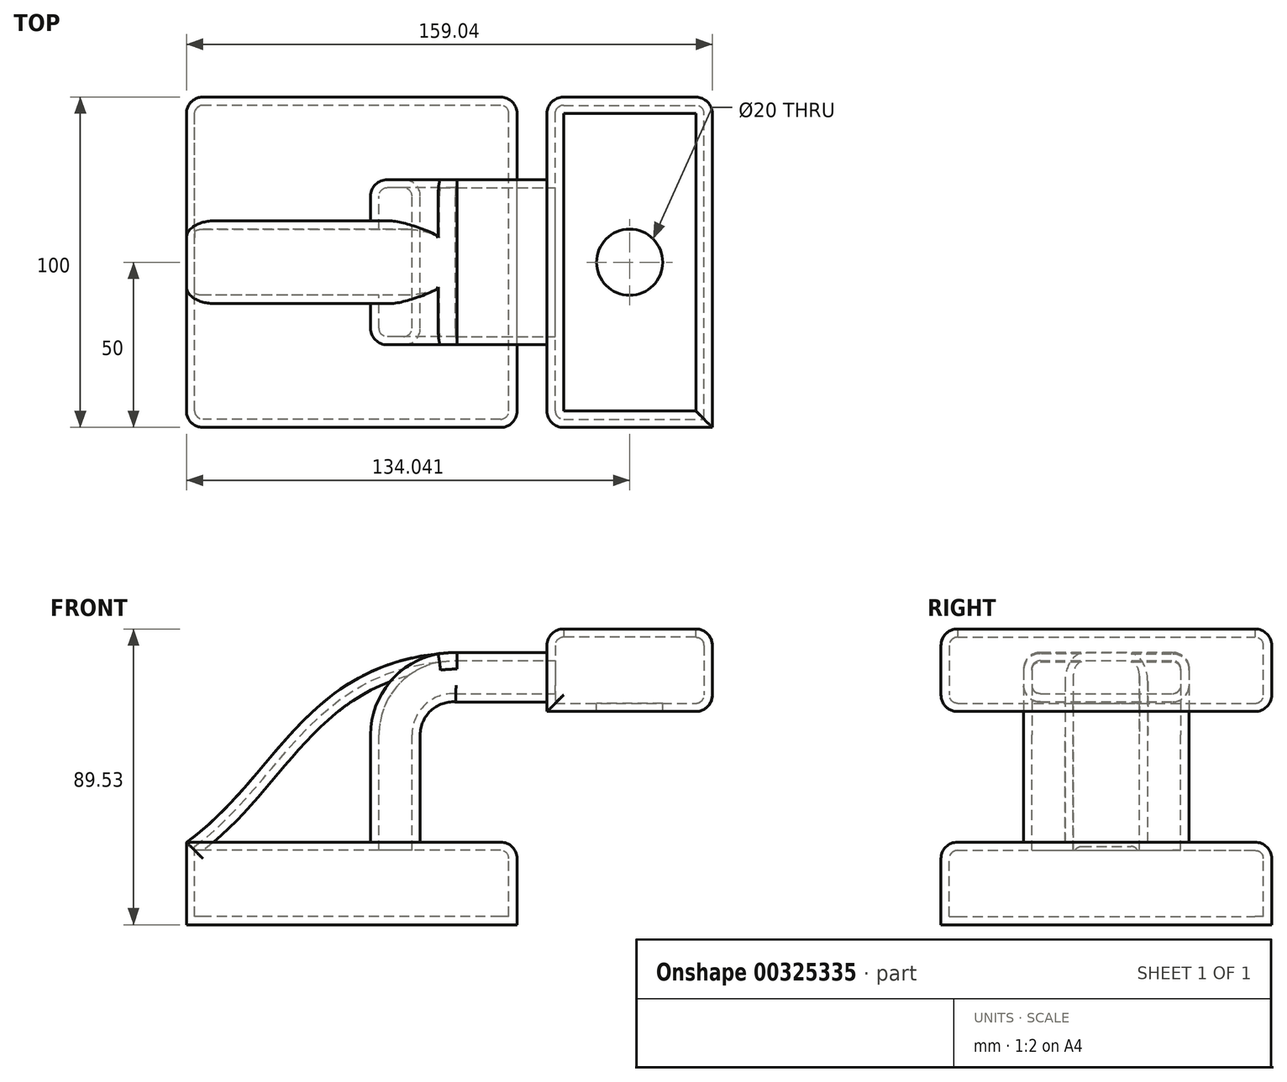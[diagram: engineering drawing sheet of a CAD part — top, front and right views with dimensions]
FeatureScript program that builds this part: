
annotation { "Feature Type Name" : "Feature", "Feature Type Description" : "" }
export const myFeature = defineFeature(function(context is Context, id is Id, definition is map)
    precondition{}
    {
        {
            var Q0;
            Q0=qCreatedBy(makeId("Front.planeOp"),FACE);
            var sketch = newSketch(context, id + "F0", { "sketchPlane" : qUnion([Q0])});
            skLineSegment(sketch, "E0.bottom", {"start": v(50, -12.5) * mm, "end": v(-50, -12.5) * mm});
            skLineSegment(sketch, "E0.top", {"start": v(50, 12.5) * mm, "end": v(-50, 12.5) * mm});
            skLineSegment(sketch, "E0.left", {"start": v(50, -12.5) * mm, "end": v(50, 12.5) * mm});
            skLineSegment(sketch, "E0.right", {"start": v(-50, -12.5) * mm, "end": v(-50, 12.5) * mm});
            skPoint(sketch, "E0.middle", {"position": v(0, 0) * mm});
            skLineSegment(sketch, "E1.bottom", {"start": v(59.04, 77.03) * mm, "end": v(109.04, 77.03) * mm});
            skLineSegment(sketch, "E1.top", {"start": v(59.04, 52.03) * mm, "end": v(109.04, 52.03) * mm});
            skLineSegment(sketch, "E1.left", {"start": v(59.04, 77.03) * mm, "end": v(59.04, 52.03) * mm});
            skLineSegment(sketch, "E1.right", {"start": v(109.04, 77.03) * mm, "end": v(109.04, 52.03) * mm});
            skPoint(sketch, "E1.middle", {"position": v(84.04, 64.53) * mm});
            skLineSegment(sketch, "E2", {"start": v(20.7, 12.5) * mm, "end": v(20.7, 44.96) * mm});
            skArc(sketch, "E3", {"start": v(20.7, 44.96) * mm, "mid": v(23.88, 52.27) * mm, "end": v(31.4, 54.94) * mm});
            skLineSegment(sketch, "E4", {"start": v(31.4, 54.94) * mm, "end": v(59.04, 54.94) * mm});
            skLineSegment(sketch, "E5.0", {"start": v(31.8, 69.94) * mm, "end": v(59.04, 69.94) * mm});
            skArc(sketch, "E5.1", {"start": v(5.7, 44.96) * mm, "mid": v(13.42, 63.02) * mm, "end": v(31.8, 69.94) * mm});
            skLineSegment(sketch, "E5.2", {"start": v(5.7, 12.5) * mm, "end": v(5.7, 44.96) * mm});
            skFitSpline(sketch, "E6", {"points": [v(-50, 12.5) * mm, v(31.8, 69.94) * mm], "startDerivative": vector(81.8, 57.44) * mm, "endDerivative": vector(137.66, 4.95) * mm});
            skSolve(sketch);
        }
        {
            var Q0;
            Q0=makeQuery(id+"F0.imprint","IMPRINT",FACE,{"disambiguationData":[TD([[makeQuery(id+"F0.imprint","IMPRINT",EDGE,{"derivedFrom":sQuery(id+"F0.wireOp",EDGE,"E0.bottom")}),-1.0]])]});
            extrude(context, id + "F1", {"entities" : qUnion([Q0]), "depth" : 100 * mm, "symmetric" : true});
        }
        {
            var Q0;
            {var subQ0=sQuery(id+"F0.wireOp",EDGE,"E2");Q0=makeQuery(id+"F0.imprint","IMPRINT",FACE,{"disambiguationData":[TD([[makeQuery(id+"F0.imprint","IMPRINT",EDGE,{"derivedFrom":subQ0}),1.0]])]});}
            extrude(context, id + "F2", {"entities" : qUnion([Q0]), "operationType" : NewBodyOperationType.ADD, "depth" : 50 * mm, "symmetric" : true});
        }
        {
            var Q0;
            {var subQ3=sQuery(id+"F0.wireOp",EDGE,"E5.2");Q0=makeQuery(id+"F0.imprint","IMPRINT",FACE,{"disambiguationData":[TD([[makeQuery(id+"F0.imprint","IMPRINT",EDGE,{"derivedFrom":subQ3}),1.0]])]});}
            extrude(context, id + "F3", {"entities" : qUnion([Q0]), "operationType" : NewBodyOperationType.ADD, "depth" : 25 * mm, "symmetric" : true});
        }
        {
            var Q0;
            {var subQ3=sQuery(id+"F0.wireOp",EDGE,"E1.bottom");Q0=makeQuery(id+"F0.imprint","IMPRINT",FACE,{"disambiguationData":[TD([[makeQuery(id+"F0.imprint","IMPRINT",EDGE,{"derivedFrom":subQ3}),-1.0]])]});}
            extrude(context, id + "F4", {"entities" : qUnion([Q0]), "operationType" : NewBodyOperationType.ADD, "depth" : 100 * mm, "symmetric" : true});
        }
        {
            var Q0;
            Q0=makeQuery(id+"F1.opExtrude","CAP_EDGE",EDGE,{"disambiguationData":[OSD([sQuery(id+"F0.wireOp",EDGE,"E0.right")])],"isStart":false});
            var Q1;
            Q1=makeQuery(id+"F1.opExtrude","CAP_EDGE",EDGE,{"disambiguationData":[OSD([sQuery(id+"F0.wireOp",EDGE,"E0.left")])],"isStart":false});
            var Q2;
            Q2=makeQuery(id+"F1.opExtrude","CAP_EDGE",EDGE,{"disambiguationData":[OSD([sQuery(id+"F0.wireOp",EDGE,"E0.left")])],"isStart":true});
            var Q3;
            Q3=makeQuery(id+"F1.opExtrude","CAP_EDGE",EDGE,{"disambiguationData":[OSD([sQuery(id+"F0.wireOp",EDGE,"E0.right")])],"isStart":true});
            var Q4;
            Q4=makeQuery(id+"F4.opExtrude","CAP_EDGE",EDGE,{"disambiguationData":[OSD([sQuery(id+"F0.wireOp",EDGE,"E1.left")])],"isStart":true});
            var Q5;
            Q5=makeQuery(id+"F4.opExtrude","CAP_EDGE",EDGE,{"disambiguationData":[OSD([sQuery(id+"F0.wireOp",EDGE,"E1.right")])],"isStart":true});
            var Q6;
            Q6=makeQuery(id+"F4.opExtrude","CAP_EDGE",EDGE,{"disambiguationData":[OSD([sQuery(id+"F0.wireOp",EDGE,"E1.left")])],"isStart":false});
            var Q7;
            Q7=makeQuery(id+"F2.opExtrude","CAP_EDGE",EDGE,{"disambiguationData":[OSD([sQuery(id+"F0.wireOp",EDGE,"E5.0")])],"isStart":true});
            var Q8;
            Q8=makeQuery(id+"F2.opExtrude","CAP_EDGE",EDGE,{"disambiguationData":[OSD([sQuery(id+"F0.wireOp",EDGE,"E5.1")])],"isStart":true});
            var Q9;
            Q9=makeQuery(id+"F3.opExtrude","CAP_EDGE",EDGE,{"disambiguationData":[OSD([sQuery(id+"F0.wireOp",EDGE,"E6")])],"isStart":true});
            var Q10;
            Q10=makeQuery(id+"F3.opExtrude","CAP_EDGE",EDGE,{"disambiguationData":[OSD([sQuery(id+"F0.wireOp",EDGE,"E6")])],"isStart":false});
            var Q11;
            Q11=makeQuery(id+"F4.opExtrude","CAP_EDGE",EDGE,{"disambiguationData":[OSD([sQuery(id+"F0.wireOp",EDGE,"E1.bottom")])],"isStart":true});
            var Q12;
            Q12=makeQuery(id+"F4.opExtrude","SWEPT_EDGE",EDGE,{"disambiguationData":[OSD([sQuery(id+"F0.wireOp",EDGE,"E1.bottom"),sQuery(id+"F0.wireOp",EDGE,"E1.left")])]});
            var Q13;
            Q13=makeQuery(id+"F4.opExtrude","SWEPT_EDGE",EDGE,{"disambiguationData":[OSD([sQuery(id+"F0.wireOp",EDGE,"E1.bottom"),sQuery(id+"F0.wireOp",EDGE,"E1.right")])]});
            var Q14;
            Q14=makeQuery(id+"F4.opExtrude","CAP_EDGE",EDGE,{"disambiguationData":[OSD([sQuery(id+"F0.wireOp",EDGE,"E1.bottom")])],"isStart":false});
            var Q15;
            Q15=makeQuery(id+"F2.opExtrude","CAP_EDGE",EDGE,{"disambiguationData":[OSD([sQuery(id+"F0.wireOp",EDGE,"E5.0")])],"isStart":false});
            var Q16;
            Q16=makeQuery(id+"F2.opExtrude","CAP_EDGE",EDGE,{"disambiguationData":[OSD([sQuery(id+"F0.wireOp",EDGE,"E5.1")])],"isStart":false});
            var Q17;
            Q17=makeQuery(id+"F2.opExtrude","CAP_EDGE",EDGE,{"disambiguationData":[OSD([sQuery(id+"F0.wireOp",EDGE,"E2")])],"isStart":false});
            var Q18;
            Q18=makeQuery(id+"F2.opExtrude","CAP_EDGE",EDGE,{"disambiguationData":[OSD([sQuery(id+"F0.wireOp",EDGE,"E4")])],"isStart":false});
            var Q19;
            Q19=makeQuery(id+"F1.opExtrude","CAP_EDGE",EDGE,{"disambiguationData":[OSD([sQuery(id+"F0.wireOp",EDGE,"E0.top")])],"isStart":false});
            var Q20;
            Q20=makeQuery(id+"F1.opExtrude","SWEPT_EDGE",EDGE,{"disambiguationData":[OSD([sQuery(id+"F0.wireOp",EDGE,"E0.top"),sQuery(id+"F0.wireOp",EDGE,"E0.left")])]});
            var Q21;
            Q21=makeQuery(id+"F4.opExtrude","CAP_EDGE",EDGE,{"disambiguationData":[OSD([sQuery(id+"F0.wireOp",EDGE,"E1.top")])],"isStart":false});
            var Q22;
            Q22=makeQuery(id+"F4.opExtrude","SWEPT_EDGE",EDGE,{"disambiguationData":[OSD([sQuery(id+"F0.wireOp",EDGE,"E1.top"),sQuery(id+"F0.wireOp",EDGE,"E1.right")])]});
            var Q23;
            Q23=makeQuery(id+"F4.opExtrude","CAP_EDGE",EDGE,{"disambiguationData":[OSD([sQuery(id+"F0.wireOp",EDGE,"E1.top")])],"isStart":true});
            var Q24;
            Q24=makeQuery(id+"F1.opExtrude","CAP_EDGE",EDGE,{"disambiguationData":[OSD([sQuery(id+"F0.wireOp",EDGE,"E0.top")])],"isStart":true});
            var Q25;
            Q25=makeQuery(id+"F2.opExtrude","CAP_EDGE",EDGE,{"disambiguationData":[OSD([sQuery(id+"F0.wireOp",EDGE,"E2")])],"isStart":true});
            var Q26;
            Q26=makeQuery(id+"F2.opExtrude","CAP_EDGE",EDGE,{"disambiguationData":[OSD([sQuery(id+"F0.wireOp",EDGE,"E4")])],"isStart":true});
            fillet(context, id + "F5", {"entities" : qUnion([Q0, Q1, Q2, Q3, Q4, Q5, Q6, Q7, Q8, Q9, Q10, Q11, Q12, Q13, Q14, Q15, Q16, Q17, Q18, Q19, Q20, Q21, Q22, Q23, Q24, Q25, Q26]), "radius" : 5 * mm, "tangentPropagation" : true, "allowEdgeOverflow" : false});
        }
        {
            var Q0;
            Q0=makeQuery(id+"F4.opExtrude","SWEPT_FACE",FACE,{"disambiguationData":[OSD([sQuery(id+"F0.wireOp",EDGE,"E1.bottom")])]});
            shell(context, id + "F6", {"entities" : qUnion([Q0]), "thickness" : 2.5 * mm});
        }
        {
            var Q0;
            Q0=qCreatedBy(makeId("Top.planeOp"),FACE);
            var sketch = newSketch(context, id + "F7", { "sketchPlane" : qUnion([Q0])});
            skCircle(sketch, "E7", {"center": v(84.04, 0) * mm, "radius": 10 * mm});
            skSolve(sketch);
        }
        {
            var Q0;
            Q0=sQuery(id+"F7.wireOp",VERTEX,"E7.center");
            var Q1;
            Q1=makeQuery(id+"F1.opExtrude","SWEPT_BODY",BODY,{"disambiguationData":[OSD([sQuery(id+"F0.wireOp",EDGE,"E0.bottom"),sQuery(id+"F0.wireOp",EDGE,"E0.top"),sQuery(id+"F0.wireOp",EDGE,"E0.left"),sQuery(id+"F0.wireOp",EDGE,"E0.right")])]});
            hole(context, id + "F8", {"style" : HoleStyle.SIMPLE, "endStyle" : HoleEndStyle.THROUGH, "oppositeDirection" : true, "holeDiameter" : 20 * mm, "tappedDepth" : 12 * mm, "tapClearance" : 3, "locations" : qUnion([Q0]), "scope" : qUnion([Q1])});
        }
    });
